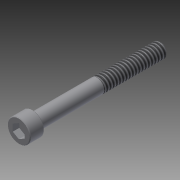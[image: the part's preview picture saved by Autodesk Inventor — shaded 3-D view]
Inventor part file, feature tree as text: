
AUTODESK INVENTOR PART (.ipt)
format: ipt  version: 2014 SP2 (Build 180246200, 246)  size: 111,616 bytes
history: native  units: in
note: dims shown in document units (in); Inventor stores cm internally (conversion verified against a paired STEP export)
features: other x7, sketch x2, revolve x1, thread x1, extrude x1
ambient origin geometry x8: Origin, YZ Plane, XZ Plane, XY Plane, X Axis, Y Axis, Z Axis, Center Point
bodies: Solid1 (feature_tree)
feature tree (12):
  revolve  "Revolution1"  [1 undecoded]
  thread  "Thread1"  [1 undecoded]
  extrude  "Extrusion1"  [1 undecoded]
  other  "screw_XY"
  other  "screw_YZ"
  other  "screw_ZX"
  other  "screw_X"
  other  "screw_Y"
  other  "screw_Z"
  other  "screw_Center"
  sketch  "Sketch_1"  dims[d0=360.0deg d1=0.4851in d2=0.0in d3=0.051in d4=0.0in]
  sketch  "Sketch_3"  dims[d5=0.0in]
note: 3 required parameter values undecoded (feature->parameter linkage not recoverable at this tier; creation-order binding heuristic only, values carry confidence <= 0.55)